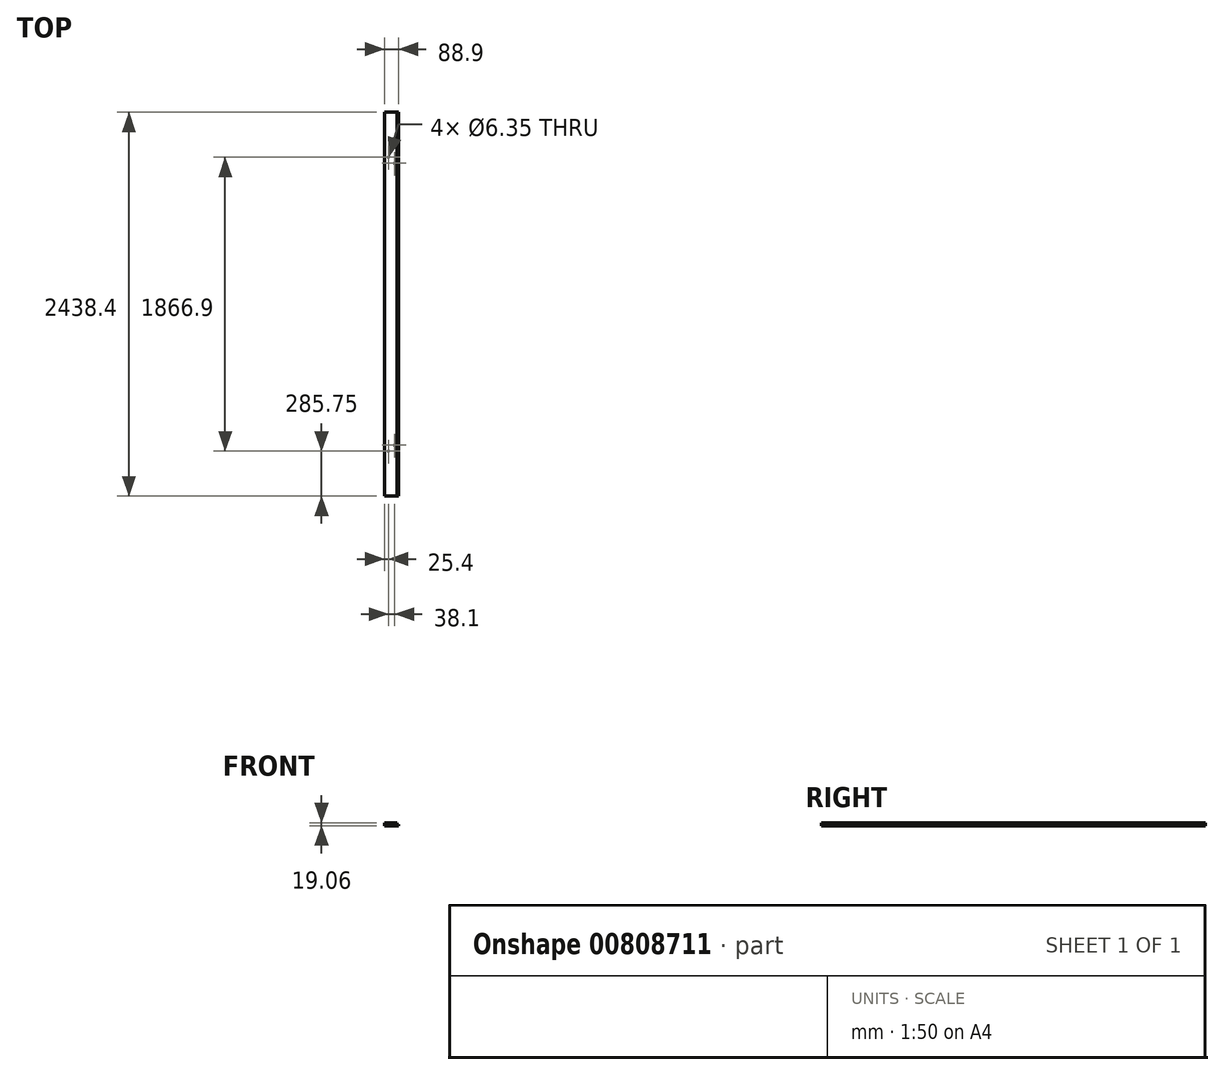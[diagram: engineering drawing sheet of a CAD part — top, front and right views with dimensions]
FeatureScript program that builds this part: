
annotation { "Feature Type Name" : "Feature", "Feature Type Description" : "" }
export const myFeature = defineFeature(function(context is Context, id is Id, definition is map)
    precondition{}
    {
        {
            var Q0;
            Q0=qCreatedBy(makeId("Front.planeOp"),FACE);
            var sketch = newSketch(context, id + "F0", { "sketchPlane" : qUnion([Q0])});
            skLineSegment(sketch, "E0.bottom", {"start": v(-44.45, 9.52) * mm, "end": v(44.45, 9.52) * mm});
            skLineSegment(sketch, "E0.top", {"start": v(-44.45, -9.52) * mm, "end": v(44.45, -9.52) * mm});
            skLineSegment(sketch, "E0.left", {"start": v(-44.45, 9.52) * mm, "end": v(-44.45, -9.53) * mm});
            skLineSegment(sketch, "E0.right", {"start": v(44.45, 9.52) * mm, "end": v(44.45, -9.53) * mm});
            skLineSegment(sketch, "E1", {"start": v(-44.45, -9.53) * mm, "end": v(44.45, 9.53) * mm, "construction": true});
            skSolve(sketch);
        }
        {
            var Q0;
            Q0=qSketchRegion(id+"F0",true);
            extrude(context, id + "F1", {"entities" : qUnion([Q0]), "depth" : 2438.4 * mm, "offsetDistance" : 25.4 * mm, "symmetric" : true});
        }
        {
            var Q0;
            Q0=makeQuery(id+"F1.opExtrude","CAP_FACE",FACE,{"disambiguationData":[OSD([sQuery(id+"F0.wireOp",EDGE,"E0.bottom"),sQuery(id+"F0.wireOp",EDGE,"E0.top"),sQuery(id+"F0.wireOp",EDGE,"E0.left"),sQuery(id+"F0.wireOp",EDGE,"E0.right")])],"isStart":false});
            var sketch = newSketch(context, id + "F2", { "sketchPlane" : qUnion([Q0])});
            skLineSegment(sketch, "E2.bottom", {"start": v(34.93, 22) * mm, "end": v(79.08, 22) * mm});
            skLineSegment(sketch, "E2.top", {"start": v(34.93, 0) * mm, "end": v(79.08, 0) * mm});
            skLineSegment(sketch, "E2.left", {"start": v(34.93, 22) * mm, "end": v(34.93, 0) * mm});
            skLineSegment(sketch, "E2.right", {"start": v(79.08, 22) * mm, "end": v(79.08, 0) * mm});
            skSolve(sketch);
        }
        {
            var Q0;
            Q0=qSketchRegion(id+"F2",true);
            extrude(context, id + "F3", {"entities" : qUnion([Q0]), "operationType" : NewBodyOperationType.REMOVE, "endBound" : BoundingType.THROUGH_ALL, "oppositeDirection" : true, "depth" : 25.4 * mm, "offsetDistance" : 25.4 * mm});
        }
        {
            var Q0;
            Q0=makeQuery(id+"F1.opExtrude","SWEPT_FACE",FACE,{"disambiguationData":[OSD([sQuery(id+"F0.wireOp",EDGE,"E0.bottom")])]});
            var sketch = newSketch(context, id + "F4", { "sketchPlane" : qUnion([Q0])});
            skLineSegment(sketch, "E3", {"start": v(6.28, -12.65) * mm, "end": v(0, -385.82) * mm});
            skLineSegment(sketch, "E4", {"start": v(-33.61, -385.82) * mm, "end": v(16.98, -401.5) * mm});
            skSolve(sketch);
        }
        {
            var Q0;
            {var subQ0=sQuery(id+"F0.wireOp",EDGE,"E0.bottom");Q0=makeQuery(id+"F4.imprint","IMPRINT",FACE,{"disambiguationData":[TD([[makeQuery(id+"F4.imprint","IMPRINT",EDGE,{"derivedFrom":makeQuery(id+"F1.opExtrude","CAP_EDGE",EDGE,{"disambiguationData":[OSD([subQ0])],"isStart":true})}),-1.0]])]});}
            var sketch = newSketch(context, id + "F5", { "sketchPlane" : qUnion([Q0])});
            skLineSegment(sketch, "E5.bottom", {"start": v(-19.05, -895.35) * mm, "end": v(19.05, -895.35) * mm, "construction": true});
            skLineSegment(sketch, "E5.top", {"start": v(-19.05, -933.45) * mm, "end": v(19.05, -933.45) * mm, "construction": true});
            skLineSegment(sketch, "E5.left", {"start": v(-19.05, -895.35) * mm, "end": v(-19.05, -933.45) * mm, "construction": true});
            skLineSegment(sketch, "E5.right", {"start": v(19.05, -895.35) * mm, "end": v(19.05, -933.45) * mm, "construction": true});
            skLineSegment(sketch, "E6", {"start": v(0, 0) * mm, "end": v(0, -895.35) * mm, "construction": true});
            skLineSegment(sketch, "E7", {"start": v(0, 0) * mm, "end": v(78.34, 0) * mm, "construction": true});
            skCircle(sketch, "E8", {"center": v(19.05, -895.35) * mm, "radius": 3.18 * mm});
            skCircle(sketch, "E9", {"center": v(-19.05, -933.45) * mm, "radius": 3.18 * mm});
            skCircle(sketch, "E10.MirrorC", {"center": v(-19.05, 933.45) * mm, "radius": 3.18 * mm});
            skCircle(sketch, "E11.MirrorC", {"center": v(19.05, 895.35) * mm, "radius": 3.18 * mm});
            skSolve(sketch);
        }
        {
            var Q0;
            Q0 = qSketchRegion(id + "F5", true);
            extrude(context, id + "F6", {"entities" : qUnion([Q0]), "operationType" : NewBodyOperationType.REMOVE, "endBound" : BoundingType.UP_TO_NEXT, "oppositeDirection" : true, "depth" : 25.4 * mm, "offsetDistance" : 25.4 * mm});
        }
    });
